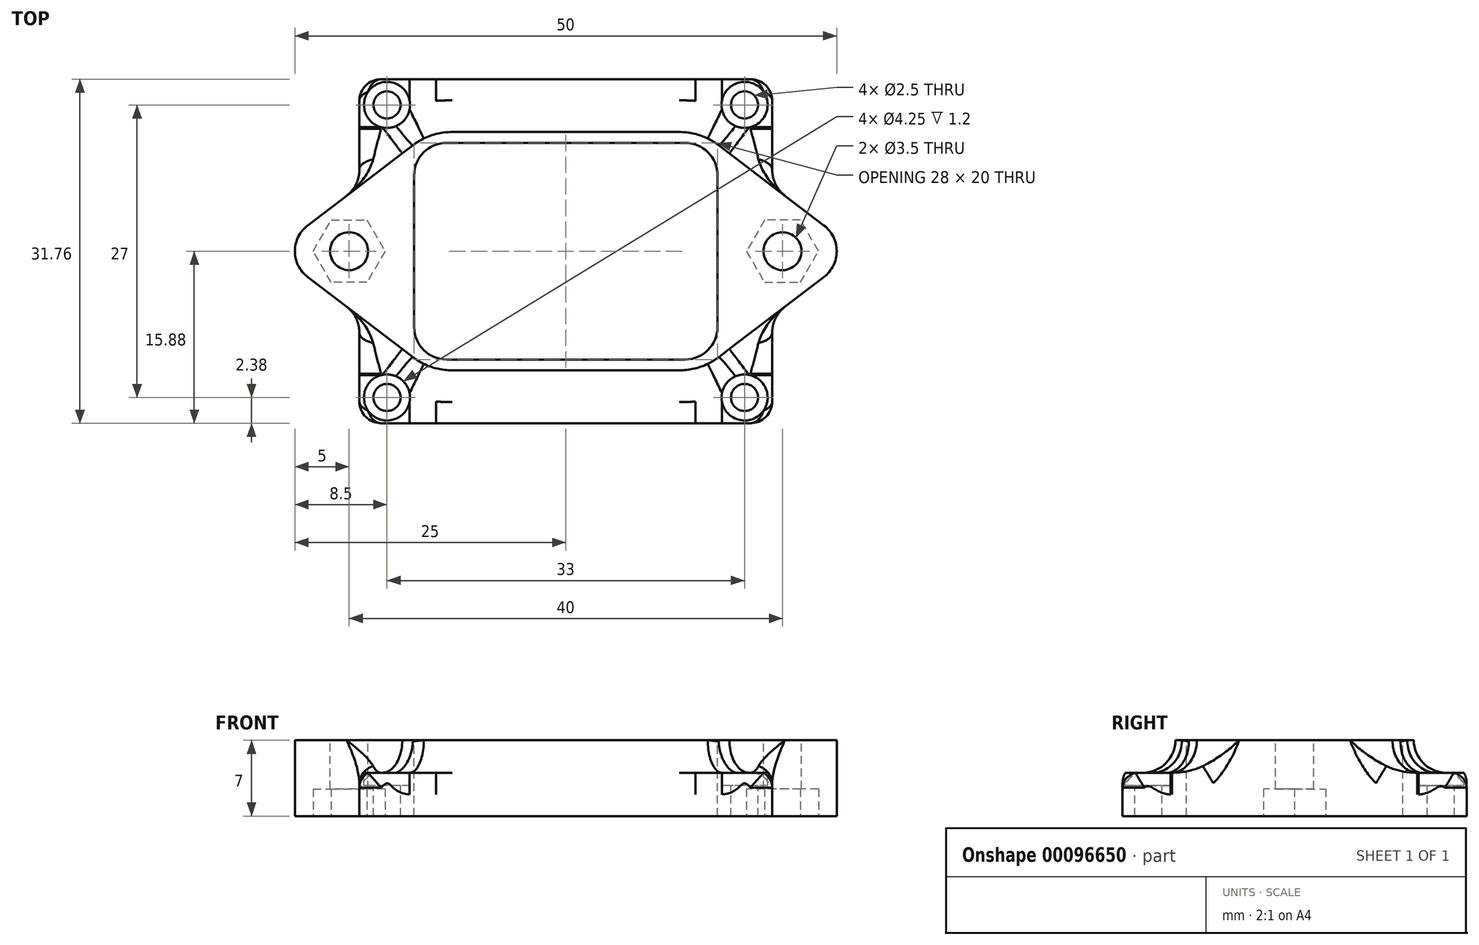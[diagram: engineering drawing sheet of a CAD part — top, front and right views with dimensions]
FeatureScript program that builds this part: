
annotation { "Feature Type Name" : "Feature", "Feature Type Description" : "" }
export const myFeature = defineFeature(function(context is Context, id is Id, definition is map)
    precondition{}
    {
        {
            var Q0;
            Q0=qCreatedBy(makeId("Top.planeOp"),FACE);
            var sketch = newSketch(context, id + "F0", { "sketchPlane" : qUnion([Q0])});
            skLineSegment(sketch, "E0.bottom", {"start": v(-19.05, 15.88) * mm, "end": v(19.05, 15.88) * mm});
            skLineSegment(sketch, "E0.top", {"start": v(-19.05, -15.88) * mm, "end": v(19.05, -15.88) * mm});
            skLineSegment(sketch, "E0.left", {"start": v(-19.05, 15.87) * mm, "end": v(-19.05, -15.88) * mm});
            skLineSegment(sketch, "E0.right", {"start": v(19.05, 15.87) * mm, "end": v(19.05, -15.88) * mm});
            skPoint(sketch, "E0.middle", {"position": v(0, 0) * mm});
            skSolve(sketch);
        }
        {
            var Q0;
            Q0 = qSketchRegion(id + "F0", true);
            extrude(context, id + "F1", {"entities" : qUnion([Q0]), "depth" : 4 * mm});
        }
        {
            var Q0;
            Q0=qCreatedBy(makeId("Top.planeOp"),FACE);
            var sketch = newSketch(context, id + "F2", { "sketchPlane" : qUnion([Q0])});
            skLineSegment(sketch, "E1.bottom", {"start": v(-10.48, 11) * mm, "end": v(10.48, 11) * mm});
            skLineSegment(sketch, "E1.top", {"start": v(-10.48, -11) * mm, "end": v(10.48, -11) * mm});
            skPoint(sketch, "E1.middle", {"position": v(0, 0) * mm});
            skLineSegment(sketch, "E2", {"start": v(-14.11, 9.77) * mm, "end": v(-23.82, 2.39) * mm});
            skLineSegment(sketch, "E3", {"start": v(-23.82, -2.39) * mm, "end": v(-14.11, -9.77) * mm});
            skLineSegment(sketch, "E4", {"start": v(-12.5, -11) * mm, "end": v(-12.5, 11) * mm, "construction": true});
            skArc(sketch, "E5.filletArc", {"start": v(-23.82, 2.39) * mm, "mid": v(-25, 0) * mm, "end": v(-23.82, -2.39) * mm});
            skLineSegment(sketch, "E6.MirrorCS", {"start": v(14.11, 9.77) * mm, "end": v(23.82, 2.39) * mm});
            skLineSegment(sketch, "E7.MirrorCS", {"start": v(23.82, -2.39) * mm, "end": v(14.11, -9.77) * mm});
            skArc(sketch, "E8.MirrorCS", {"start": v(23.82, 2.39) * mm, "mid": v(25, 0) * mm, "end": v(23.82, -2.39) * mm});
            skLineSegment(sketch, "E9", {"start": v(12.5, 11) * mm, "end": v(12.5, -11) * mm, "construction": true});
            skPoint(sketch, "E10.visualSharp", {"position": v(-12.5, 11) * mm});
            skArc(sketch, "E10.filletArc", {"start": v(-10.48, 11) * mm, "mid": v(-12.4, 10.69) * mm, "end": v(-14.11, 9.77) * mm});
            skPoint(sketch, "E11.visualSharp", {"position": v(12.5, 11) * mm});
            skArc(sketch, "E11.filletArc", {"start": v(14.11, 9.77) * mm, "mid": v(12.4, 10.69) * mm, "end": v(10.48, 11) * mm});
            skPoint(sketch, "E12.visualSharp", {"position": v(12.5, -11) * mm});
            skArc(sketch, "E12.filletArc", {"start": v(10.48, -11) * mm, "mid": v(12.4, -10.69) * mm, "end": v(14.11, -9.77) * mm});
            skPoint(sketch, "E13.visualSharp", {"position": v(-12.5, -11) * mm});
            skArc(sketch, "E13.filletArc", {"start": v(-14.11, -9.77) * mm, "mid": v(-12.4, -10.69) * mm, "end": v(-10.48, -11) * mm});
            skSolve(sketch);
        }
        {
            var Q0;
            Q0 = qSketchRegion(id + "F2", true);
            extrude(context, id + "F3", {"entities" : qUnion([Q0]), "operationType" : NewBodyOperationType.ADD, "depth" : 7 * mm});
        }
        {
            var Q0;
            Q0=makeQuery(id+"F3.opExtrude","CAP_FACE",FACE,{"disambiguationData":[OSD([sQuery(id+"F2.wireOp",EDGE,"E1.bottom"),sQuery(id+"F2.wireOp",EDGE,"E1.top"),sQuery(id+"F2.wireOp",EDGE,"E1.left"),sQuery(id+"F2.wireOp",EDGE,"E1.right")])],"isStart":false});
            var sketch = newSketch(context, id + "F4", { "sketchPlane" : qUnion([Q0])});
            skLineSegment(sketch, "E14.bottom", {"start": v(11, 10) * mm, "end": v(-11, 10) * mm});
            skLineSegment(sketch, "E14.top", {"start": v(11, -10) * mm, "end": v(-11, -10) * mm});
            skLineSegment(sketch, "E14.left", {"start": v(14, 7) * mm, "end": v(14, -7) * mm});
            skLineSegment(sketch, "E14.right", {"start": v(-14, 7) * mm, "end": v(-14, -7) * mm});
            skPoint(sketch, "E14.middle", {"position": v(0, 0) * mm});
            skCircle(sketch, "E15", {"center": v(-20, 0) * mm, "radius": 1.75 * mm});
            skCircle(sketch, "E16.MirrorC", {"center": v(20, 0) * mm, "radius": 1.75 * mm});
            skPoint(sketch, "E17.visualSharp", {"position": v(14, 10) * mm});
            skArc(sketch, "E17.filletArc", {"start": v(14, 7) * mm, "mid": v(13.12, 9.12) * mm, "end": v(11, 10) * mm});
            skPoint(sketch, "E18.visualSharp", {"position": v(14, -10) * mm});
            skArc(sketch, "E18.filletArc", {"start": v(11, -10) * mm, "mid": v(13.12, -9.12) * mm, "end": v(14, -7) * mm});
            skPoint(sketch, "E19.visualSharp", {"position": v(-14, -10) * mm});
            skArc(sketch, "E19.filletArc", {"start": v(-14, -7) * mm, "mid": v(-13.12, -9.12) * mm, "end": v(-11, -10) * mm});
            skPoint(sketch, "E20.visualSharp", {"position": v(-14, 10) * mm});
            skArc(sketch, "E20.filletArc", {"start": v(-11, 10) * mm, "mid": v(-13.12, 9.12) * mm, "end": v(-14, 7) * mm});
            skSolve(sketch);
        }
        {
            var Q0;
            Q0 = qSketchRegion(id + "F4", true);
            extrude(context, id + "F5", {"entities" : qUnion([Q0]), "operationType" : NewBodyOperationType.REMOVE, "endBound" : BoundingType.THROUGH_ALL, "oppositeDirection" : true, "depth" : 25 * mm});
        }
        {
            var Q0;
            {var subQ0=sQuery(id+"F2.wireOp",EDGE,"E1.top");var subQ1=sQuery(id+"F2.wireOp",EDGE,"E1.bottom");var subQ2=sQuery(id+"F0.wireOp",EDGE,"E0.left");var subQ3=sQuery(id+"F2.wireOp",EDGE,"E1.left");Q0=makeQuery(id+"F3.boolean.opBoolean","SPLIT",FACE,{"disambiguationData":[TD([makeQuery(id+"F1.opExtrude","SWEPT_FACE",FACE,{"disambiguationData":[OSD([subQ2])]})])],"derivedFrom":makeQuery(id+"F3.opExtrude","CAP_FACE",FACE,{"disambiguationData":[OSD([subQ1,subQ0,subQ3,sQuery(id+"F2.wireOp",EDGE,"E1.right")])],"isStart":true})});}
            var sketch = newSketch(context, id + "F6", { "sketchPlane" : qUnion([Q0])});
            skCircle(sketch, "E21.cCircle", {"center": v(-20, 0) * mm, "radius": 2.88 * mm, "construction": true});
            skLineSegment(sketch, "E21.0", {"start": v(-21.66, 2.88) * mm, "end": v(-18.34, 2.88) * mm});
            skLineSegment(sketch, "E21.1", {"start": v(-18.34, 2.87) * mm, "end": v(-16.68, 0) * mm});
            skLineSegment(sketch, "E21.2", {"start": v(-16.68, 0) * mm, "end": v(-18.34, -2.88) * mm});
            skLineSegment(sketch, "E21.3", {"start": v(-18.34, -2.87) * mm, "end": v(-21.66, -2.88) * mm});
            skLineSegment(sketch, "E21.4", {"start": v(-21.66, -2.88) * mm, "end": v(-23.32, 0) * mm});
            skLineSegment(sketch, "E21.5", {"start": v(-23.32, 0) * mm, "end": v(-21.66, 2.87) * mm});
            skPoint(sketch, "E21.0.midPoint", {"position": v(-20, 2.88) * mm});
            skLineSegment(sketch, "E22.MirrorCS", {"start": v(21.66, 2.88) * mm, "end": v(18.34, 2.88) * mm});
            skLineSegment(sketch, "E23.MirrorCS", {"start": v(23.32, 0) * mm, "end": v(21.66, 2.87) * mm});
            skLineSegment(sketch, "E24.MirrorCS", {"start": v(21.66, -2.88) * mm, "end": v(23.32, 0) * mm});
            skLineSegment(sketch, "E25.MirrorCS", {"start": v(18.34, -2.87) * mm, "end": v(21.66, -2.88) * mm});
            skLineSegment(sketch, "E26.MirrorCS", {"start": v(18.34, 2.87) * mm, "end": v(16.68, 0) * mm});
            skLineSegment(sketch, "E27.MirrorCS", {"start": v(16.68, 0) * mm, "end": v(18.34, -2.88) * mm});
            skCircle(sketch, "E28.MirrorC", {"center": v(20, 0) * mm, "radius": 2.88 * mm, "construction": true});
            skPoint(sketch, "E29.MirrorP", {"position": v(20, 2.88) * mm});
            skSolve(sketch);
        }
        {
            var Q0;
            Q0=makeQuery(id+"F6.imprint","IMPRINT",FACE,{"disambiguationData":[TD([[makeQuery(id+"F6.imprint","IMPRINT",EDGE,{"derivedFrom":sQuery(id+"F6.wireOp",EDGE,"E22.MirrorCS")}),1.0]])]});
            var Q1;
            {var subQ16=sQuery(id+"F6.wireOp",EDGE,"E21.1");Q1=makeQuery(id+"F6.imprint","IMPRINT",FACE,{"disambiguationData":[TD([[makeQuery(id+"F6.imprint","IMPRINT",EDGE,{"derivedFrom":subQ16}),-1.0]])]});}
            var Q2;
            {var subQ12=sQuery(id+"F6.wireOp",EDGE,"E21.4");Q2=makeQuery(id+"F6.imprint","IMPRINT",FACE,{"disambiguationData":[TD([[makeQuery(id+"F6.imprint","IMPRINT",EDGE,{"derivedFrom":subQ12}),-1.0]])]});}
            extrude(context, id + "F7", {"entities" : qUnion([Q0, Q1, Q2]), "operationType" : NewBodyOperationType.REMOVE, "oppositeDirection" : true, "depth" : 2.5 * mm, "hasSecondDirection" : true, "secondDirectionBound" : SecondDirectionBoundingType.THROUGH_ALL, "secondDirectionOppositeDirection" : false, "secondDirectionDepth" : 25 * mm});
        }
        {
            var Q0;
            {var subQ0=sQuery(id+"F0.wireOp",EDGE,"E0.right");var subQ3=sQuery(id+"F0.wireOp",EDGE,"E0.left");var subQ7=sQuery(id+"F0.wireOp",EDGE,"E0.bottom");Q0=makeQuery(id+"FpmN6rqXtl1FEyE_1.opFillet","SPLIT",FACE,{"disambiguationData":[OD(1.0)],"derivedFrom":makeQuery(id+"F3.boolean.opBoolean","SPLIT",FACE,{"disambiguationData":[TD([makeQuery(id+"F1.opExtrude","SWEPT_FACE",FACE,{"disambiguationData":[OSD([subQ7])]})])],"derivedFrom":makeQuery(id+"F1.opExtrude","CAP_FACE",FACE,{"disambiguationData":[OSD([subQ7,sQuery(id+"F0.wireOp",EDGE,"E0.top"),subQ3,subQ0])],"isStart":false})})});}
            var sketch = newSketch(context, id + "F8", { "sketchPlane" : qUnion([Q0])});
            skCircle(sketch, "E30", {"center": v(-16.5, 13.5) * mm, "radius": 1.25 * mm});
            skCircle(sketch, "E31.MirrorC", {"center": v(16.5, 13.5) * mm, "radius": 1.25 * mm});
            skCircle(sketch, "E32.MirrorC", {"center": v(-16.5, -13.5) * mm, "radius": 1.25 * mm});
            skCircle(sketch, "E33.MirrorC", {"center": v(16.5, -13.5) * mm, "radius": 1.25 * mm});
            skSolve(sketch);
        }
        {
            var Q0;
            Q0=sQuery(id+"F8.wireOp",VERTEX,"E32.MirrorC.center");
            var Q1;
            Q1=sQuery(id+"F8.wireOp",VERTEX,"E33.MirrorC.center");
            var Q2;
            Q2=sQuery(id+"F8.wireOp",VERTEX,"E30.center");
            var Q3;
            Q3=sQuery(id+"F8.wireOp",VERTEX,"E31.MirrorC.center");
            var Q4;
            Q4=makeQuery(id+"F1.opExtrude","SWEPT_BODY",BODY,{"disambiguationData":[OSD([sQuery(id+"F0.wireOp",EDGE,"E0.bottom"),sQuery(id+"F0.wireOp",EDGE,"E0.top"),sQuery(id+"F0.wireOp",EDGE,"E0.left"),sQuery(id+"F0.wireOp",EDGE,"E0.right")])]});
            hole(context, id + "F9", {"style" : HoleStyle.C_BORE, "endStyle" : HoleEndStyle.THROUGH, "holeDiameter" : 2.5 * mm, "cBoreDiameter" : 4.25 * mm, "cBoreDepth" : 1.2 * mm, "locations" : qUnion([Q0, Q1, Q2, Q3]), "scope" : qUnion([Q4]), "isTappedThrough" : true});
        }
        {
            var Q0;
            Q0=makeQuery(id+"F1.opExtrude","SWEPT_EDGE",EDGE,{"disambiguationData":[OSD([sQuery(id+"F0.wireOp",EDGE,"E0.top"),sQuery(id+"F0.wireOp",EDGE,"E0.left")])]});
            var Q1;
            Q1=makeQuery(id+"F1.opExtrude","SWEPT_EDGE",EDGE,{"disambiguationData":[OSD([sQuery(id+"F0.wireOp",EDGE,"E0.top"),sQuery(id+"F0.wireOp",EDGE,"E0.right")])]});
            var Q2;
            Q2=makeQuery(id+"F1.opExtrude","SWEPT_EDGE",EDGE,{"disambiguationData":[OSD([sQuery(id+"F0.wireOp",EDGE,"E0.bottom"),sQuery(id+"F0.wireOp",EDGE,"E0.right")])]});
            var Q3;
            Q3=makeQuery(id+"F1.opExtrude","SWEPT_EDGE",EDGE,{"disambiguationData":[OSD([sQuery(id+"F0.wireOp",EDGE,"E0.bottom"),sQuery(id+"F0.wireOp",EDGE,"E0.left")])]});
            fillet(context, id + "F10", {"entities" : qUnion([Q0, Q1, Q2, Q3]), "radius" : 2 * mm, "tangentPropagation" : true, "allowEdgeOverflow" : false});
        }
        {
            var Q0;
            Q0=makeQuery(id+"F3.boolean.opBoolean","INTERSECT",EDGE,{"derivedFrom":[makeQuery(id+"F1.opExtrude","CAP_FACE",FACE,{"disambiguationData":[OSD([sQuery(id+"F0.wireOp",EDGE,"E0.bottom"),sQuery(id+"F0.wireOp",EDGE,"E0.top"),sQuery(id+"F0.wireOp",EDGE,"E0.left"),sQuery(id+"F0.wireOp",EDGE,"E0.right")])],"isStart":false}),makeQuery(id+"F3.opExtrude","SWEPT_FACE",FACE,{"disambiguationData":[OSD([sQuery(id+"F2.wireOp",EDGE,"E1.top")])]})]});
            var Q1;
            Q1=makeQuery(id+"F3.boolean.opBoolean","INTERSECT",EDGE,{"derivedFrom":[makeQuery(id+"F1.opExtrude","CAP_FACE",FACE,{"disambiguationData":[OSD([sQuery(id+"F0.wireOp",EDGE,"E0.bottom"),sQuery(id+"F0.wireOp",EDGE,"E0.top"),sQuery(id+"F0.wireOp",EDGE,"E0.left"),sQuery(id+"F0.wireOp",EDGE,"E0.right")])],"isStart":false}),makeQuery(id+"F3.opExtrude","SWEPT_FACE",FACE,{"disambiguationData":[OSD([sQuery(id+"F2.wireOp",EDGE,"E1.bottom")])]})]});
            var Q2;
            Q2=makeQuery(id+"F3.boolean.opBoolean","INTERSECT",EDGE,{"derivedFrom":[makeQuery(id+"F1.opExtrude","SWEPT_FACE",FACE,{"disambiguationData":[OSD([sQuery(id+"F0.wireOp",EDGE,"E0.left")])]}),makeQuery(id+"F3.opExtrude","SWEPT_FACE",FACE,{"disambiguationData":[OSD([sQuery(id+"F2.wireOp",EDGE,"E2")])]})]});
            var Q3;
            Q3=makeQuery(id+"F3.boolean.opBoolean","INTERSECT",EDGE,{"derivedFrom":[makeQuery(id+"F1.opExtrude","SWEPT_FACE",FACE,{"disambiguationData":[OSD([sQuery(id+"F0.wireOp",EDGE,"E0.left")])]}),makeQuery(id+"F3.opExtrude","SWEPT_FACE",FACE,{"disambiguationData":[OSD([sQuery(id+"F2.wireOp",EDGE,"E3")])]})]});
            var Q4;
            Q4=makeQuery(id+"F3.boolean.opBoolean","INTERSECT",EDGE,{"derivedFrom":[makeQuery(id+"F1.opExtrude","SWEPT_FACE",FACE,{"disambiguationData":[OSD([sQuery(id+"F0.wireOp",EDGE,"E0.right")])]}),makeQuery(id+"F3.opExtrude","SWEPT_FACE",FACE,{"disambiguationData":[OSD([sQuery(id+"F2.wireOp",EDGE,"E6.MirrorCS")])]})]});
            var Q5;
            Q5=makeQuery(id+"F3.boolean.opBoolean","INTERSECT",EDGE,{"derivedFrom":[makeQuery(id+"F1.opExtrude","SWEPT_FACE",FACE,{"disambiguationData":[OSD([sQuery(id+"F0.wireOp",EDGE,"E0.right")])]}),makeQuery(id+"F3.opExtrude","SWEPT_FACE",FACE,{"disambiguationData":[OSD([sQuery(id+"F2.wireOp",EDGE,"E7.MirrorCS")])]})]});
            fillet(context, id + "F11", {"entities" : qUnion([Q0, Q1, Q2, Q3, Q4, Q5]), "radius" : 3 * mm, "tangentPropagation" : true, "allowEdgeOverflow" : false});
        }
        {
            var Q0;
            Q0=makeQuery(id+"F1.opExtrude","CAP_EDGE",EDGE,{"disambiguationData":[OSD([sQuery(id+"F0.wireOp",EDGE,"E0.top")])],"isStart":false});
            var Q1;
            Q1=makeQuery(id+"F1.opExtrude","CAP_EDGE",EDGE,{"disambiguationData":[OSD([sQuery(id+"F0.wireOp",EDGE,"E0.bottom")])],"isStart":false});
            fillet(context, id + "F12", {"entities" : qUnion([Q0, Q1]), "radius" : 2 * mm, "tangentPropagation" : true, "allowEdgeOverflow" : false});
        }
    });
